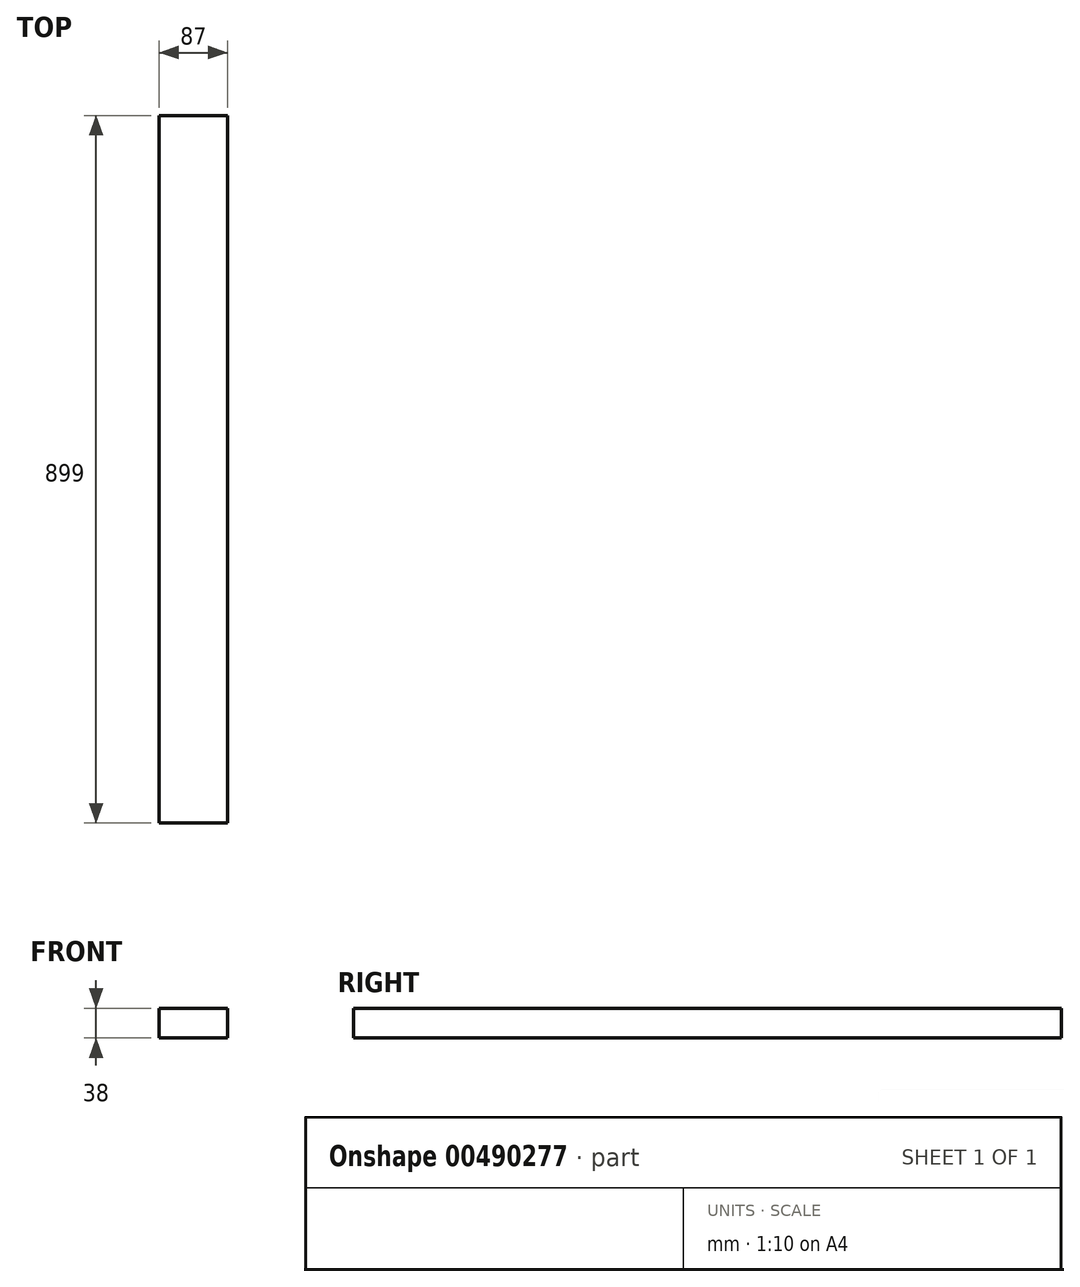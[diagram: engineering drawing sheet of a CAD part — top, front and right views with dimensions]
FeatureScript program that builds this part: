
annotation { "Feature Type Name" : "Feature", "Feature Type Description" : "" }
export const myFeature = defineFeature(function(context is Context, id is Id, definition is map)
    precondition{}
    {
        {
            var Q0;
            Q0=qCreatedBy(makeId("Front.planeOp"),FACE);
            var sketch = newSketch(context, id + "F0", { "sketchPlane" : qUnion([Q0])});
            skLineSegment(sketch, "E0.bottom", {"start": v(-46.56, 20.66) * mm, "end": v(40.44, 20.66) * mm});
            skLineSegment(sketch, "E0.top", {"start": v(-46.56, -17.34) * mm, "end": v(40.44, -17.34) * mm});
            skLineSegment(sketch, "E0.left", {"start": v(-46.56, 20.66) * mm, "end": v(-46.56, -17.34) * mm});
            skLineSegment(sketch, "E0.right", {"start": v(40.44, 20.66) * mm, "end": v(40.44, -17.34) * mm});
            skSolve(sketch);
        }
        {
            var Q0;
            Q0=makeQuery(id+"F0.imprint","IMPRINT",FACE,{"disambiguationData":[TD([[makeQuery(id+"F0.imprint","IMPRINT",EDGE,{"derivedFrom":sQuery(id+"F0.wireOp",EDGE,"E0.bottom")}),-1.0]])]});
            extrude(context, id + "F1", {"entities" : qUnion([Q0]), "depth" : 899 * mm});
        }
    });
